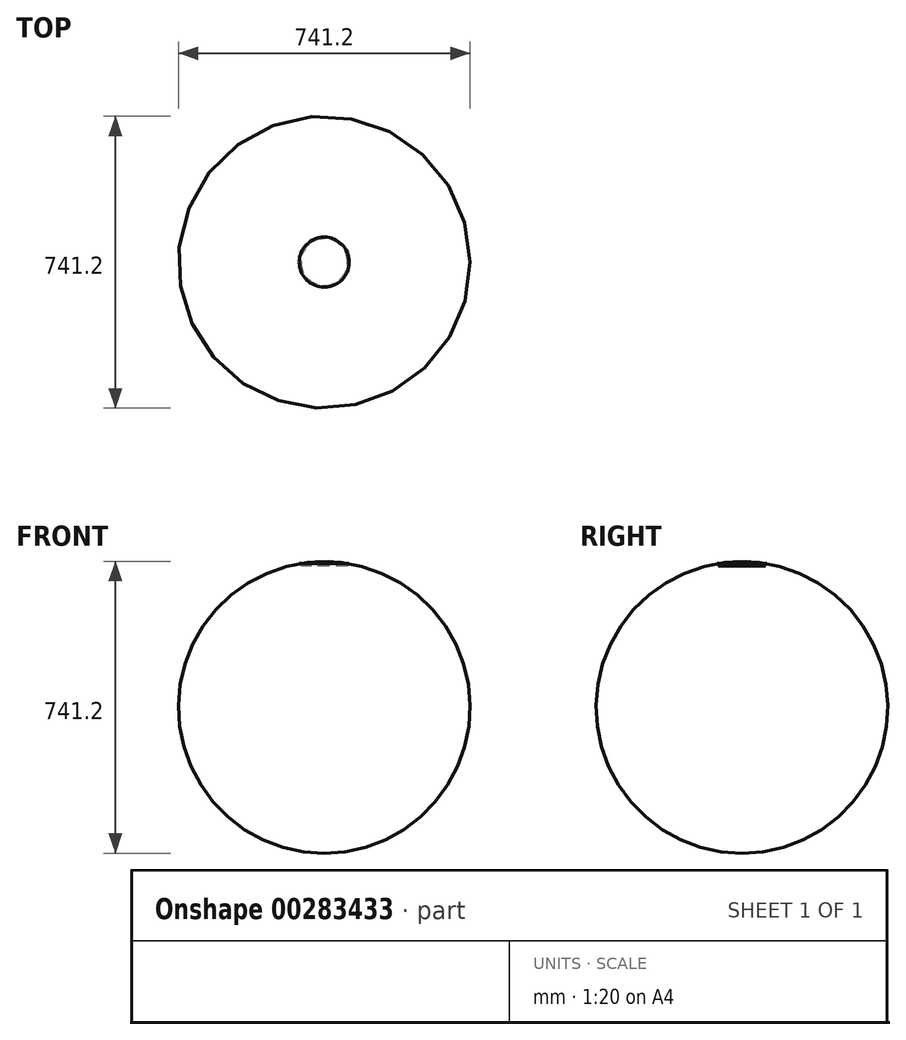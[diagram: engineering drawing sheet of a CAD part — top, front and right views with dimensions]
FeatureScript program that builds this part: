
annotation { "Feature Type Name" : "Feature", "Feature Type Description" : "" }
export const myFeature = defineFeature(function(context is Context, id is Id, definition is map)
    precondition{}
    {
        {
            var Q0;
            Q0=qCreatedBy(makeId("Top.planeOp"),FACE);
            var sketch = newSketch(context, id + "F0", { "sketchPlane" : qUnion([Q0])});
            skCircle(sketch, "E0", {"center": v(0, 0) * mm, "radius": 59.5 * mm});
            skCircle(sketch, "E1", {"center": v(0, 0) * mm, "radius": 63.5 * mm});
            skSolve(sketch);
        }
        {
            var Q0;
            Q0=makeQuery(id+"F0.imprint","IMPRINT",FACE,{"disambiguationData":[TD([[makeQuery(id+"F0.imprint","IMPRINT",EDGE,{"derivedFrom":sQuery(id+"F0.wireOp",EDGE,"E0")}),1.0]])]});
            extrude(context, id + "F1", {"entities" : qUnion([Q0]), "depth" : 4 * mm, "offsetDistance" : 25 * mm});
        }
        {
            var Q0;
            Q0=makeQuery(id+"F0.imprint","IMPRINT",FACE,{"disambiguationData":[TD([[makeQuery(id+"F0.imprint","IMPRINT",EDGE,{"derivedFrom":sQuery(id+"F0.wireOp",EDGE,"E0")}),-1.0]])]});
            var Q1;
            Q1=makeQuery(id+"F0.imprint","IMPRINT",FACE,{"disambiguationData":[TD([[makeQuery(id+"F0.imprint","IMPRINT",EDGE,{"derivedFrom":sQuery(id+"F0.wireOp",EDGE,"E0")}),1.0]])]});
            extrude(context, id + "F2", {"entities" : qUnion([Q0, Q1]), "depth" : 6 * mm, "offsetDistance" : 25 * mm, "hasSecondDirection" : true, "secondDirectionOppositeDirection" : false, "secondDirectionDepth" : 4 * mm});
        }
        {
            var Q0;
            Q0=qCreatedBy(makeId("Right.planeOp"),FACE);
            var sketch = newSketch(context, id + "F3", { "sketchPlane" : qUnion([Q0])});
            skArc(sketch, "E2", {"start": v(63.5, 6) * mm, "mid": v(0, 11.48) * mm, "end": v(-63.5, 6) * mm});
            skLineSegment(sketch, "E3", {"start": v(0, 0) * mm, "end": v(0, 32.42) * mm});
            skLineSegment(sketch, "E4", {"start": v(63.5, 6) * mm, "end": v(-63.5, 6) * mm});
            skSolve(sketch);
        }
        {
            var Q0;
            {var subQ0=sQuery(id+"F3.wireOp",EDGE,"E4");var subQ1=sQuery(id+"F3.wireOp",EDGE,"E2");var subQ2=makeQuery(id+"F3.imprint","INTERSECT",VERTEX,{"disambiguationData":[OD(1.0)],"derivedFrom":[subQ1,subQ0]});Q0=makeQuery(id+"F3.imprint","IMPRINT",FACE,{"disambiguationData":[TD([[makeQuery(id+"F3.imprint","IMPRINT",EDGE,{"disambiguationData":[TD([[subQ2,1.0]])],"derivedFrom":subQ1}),1.0]])]});}
            var Q1;
            Q1=sQuery(id+"F3.wireOp",EDGE,"E3");
            revolve(context, id + "F4", {"entities" : qUnion([Q0]), "axis" : qUnion([Q1]), "revolveType" : RevolveType.FULL});
        }
    });
